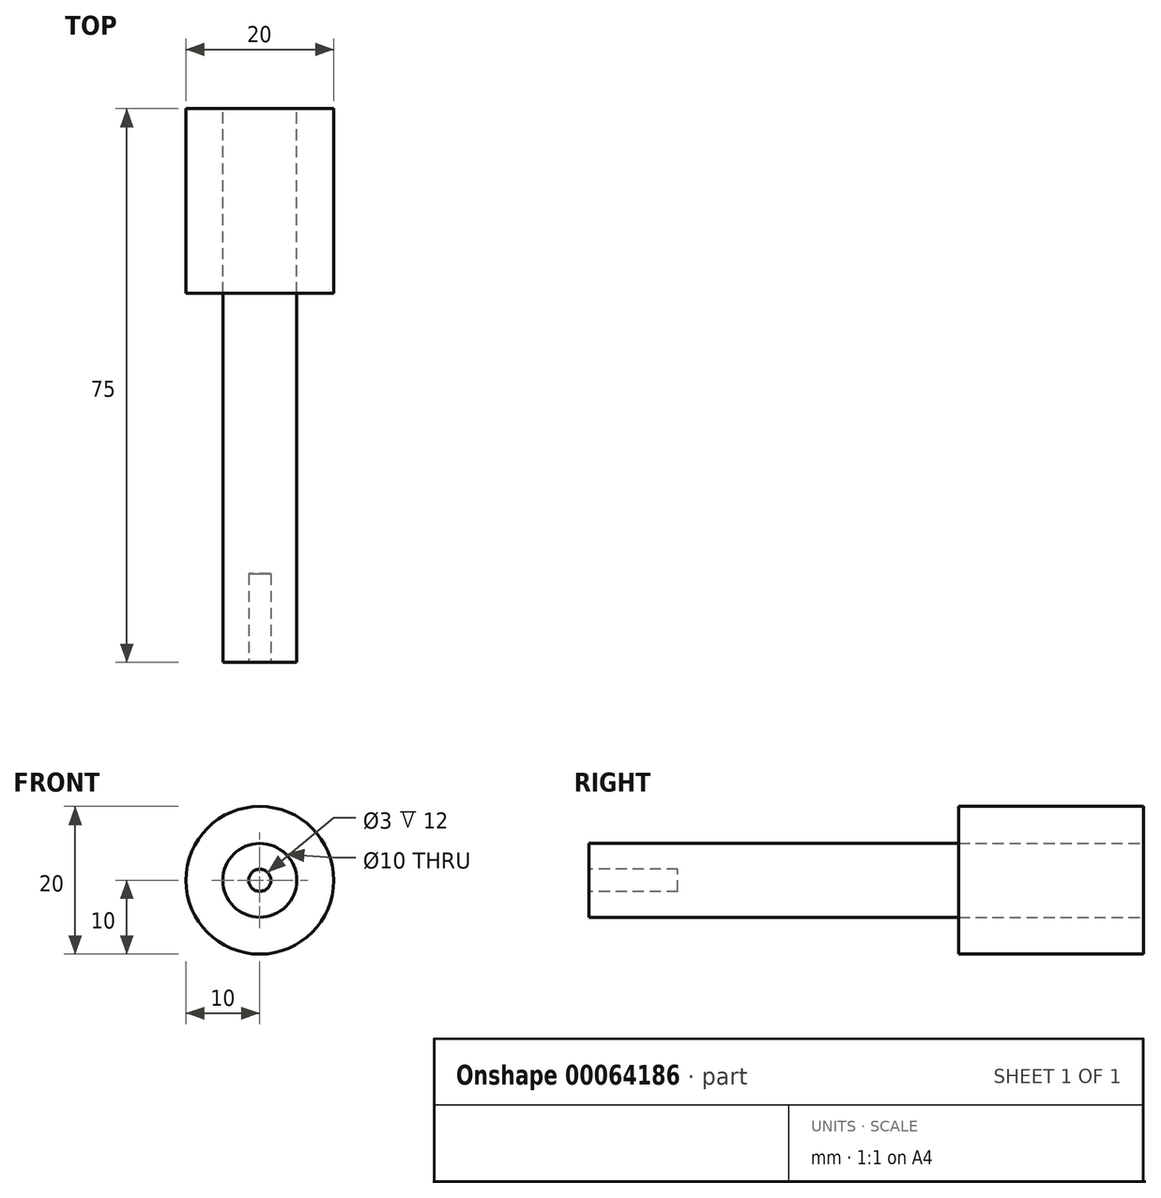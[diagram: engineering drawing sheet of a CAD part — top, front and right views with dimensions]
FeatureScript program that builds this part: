
annotation { "Feature Type Name" : "Feature", "Feature Type Description" : "" }
export const myFeature = defineFeature(function(context is Context, id is Id, definition is map)
    precondition{}
    {
        {
            var Q0;
            Q0=qCreatedBy(makeId("Front.planeOp"),FACE);
            var sketch = newSketch(context, id + "F0", { "sketchPlane" : qUnion([Q0])});
            skCircle(sketch, "E0", {"center": v(0, 0) * mm, "radius": 10 * mm});
            skCircle(sketch, "E1", {"center": v(0, 0) * mm, "radius": 5 * mm});
            skSolve(sketch);
        }
        {
            var Q0;
            Q0 = qSketchRegion(id + "F0", true);
            extrude(context, id + "F1", {"entities" : qUnion([Q0]), "depth" : 25 * mm});
        }
        {
            var Q0;
            Q0=makeQuery(id+"F1.opExtrude","CAP_FACE",FACE,{"disambiguationData":[OSD([sQuery(id+"F0.wireOp",EDGE,"E0")])],"isStart":false});
            var sketch = newSketch(context, id + "F2", { "sketchPlane" : qUnion([Q0])});
            skCircle(sketch, "E2", {"center": v(0, 0) * mm, "radius": 5 * mm});
            skSolve(sketch);
        }
        {
            var Q0;
            Q0 = qSketchRegion(id + "F2", true);
            extrude(context, id + "F3", {"entities" : qUnion([Q0]), "depth" : 50 * mm});
        }
        {
            var Q0;
            Q0=makeQuery(id+"F3.opExtrude","CAP_FACE",FACE,{"disambiguationData":[OSD([sQuery(id+"F2.wireOp",EDGE,"E2")])],"isStart":false});
            var sketch = newSketch(context, id + "F4", { "sketchPlane" : qUnion([Q0])});
            skCircle(sketch, "E3", {"center": v(0, 0) * mm, "radius": 1.5 * mm});
            skSolve(sketch);
        }
        {
            var Q0;
            Q0 = qSketchRegion(id + "F4", true);
            extrude(context, id + "F5", {"entities" : qUnion([Q0]), "operationType" : NewBodyOperationType.REMOVE, "oppositeDirection" : true, "depth" : 12 * mm});
        }
    });
